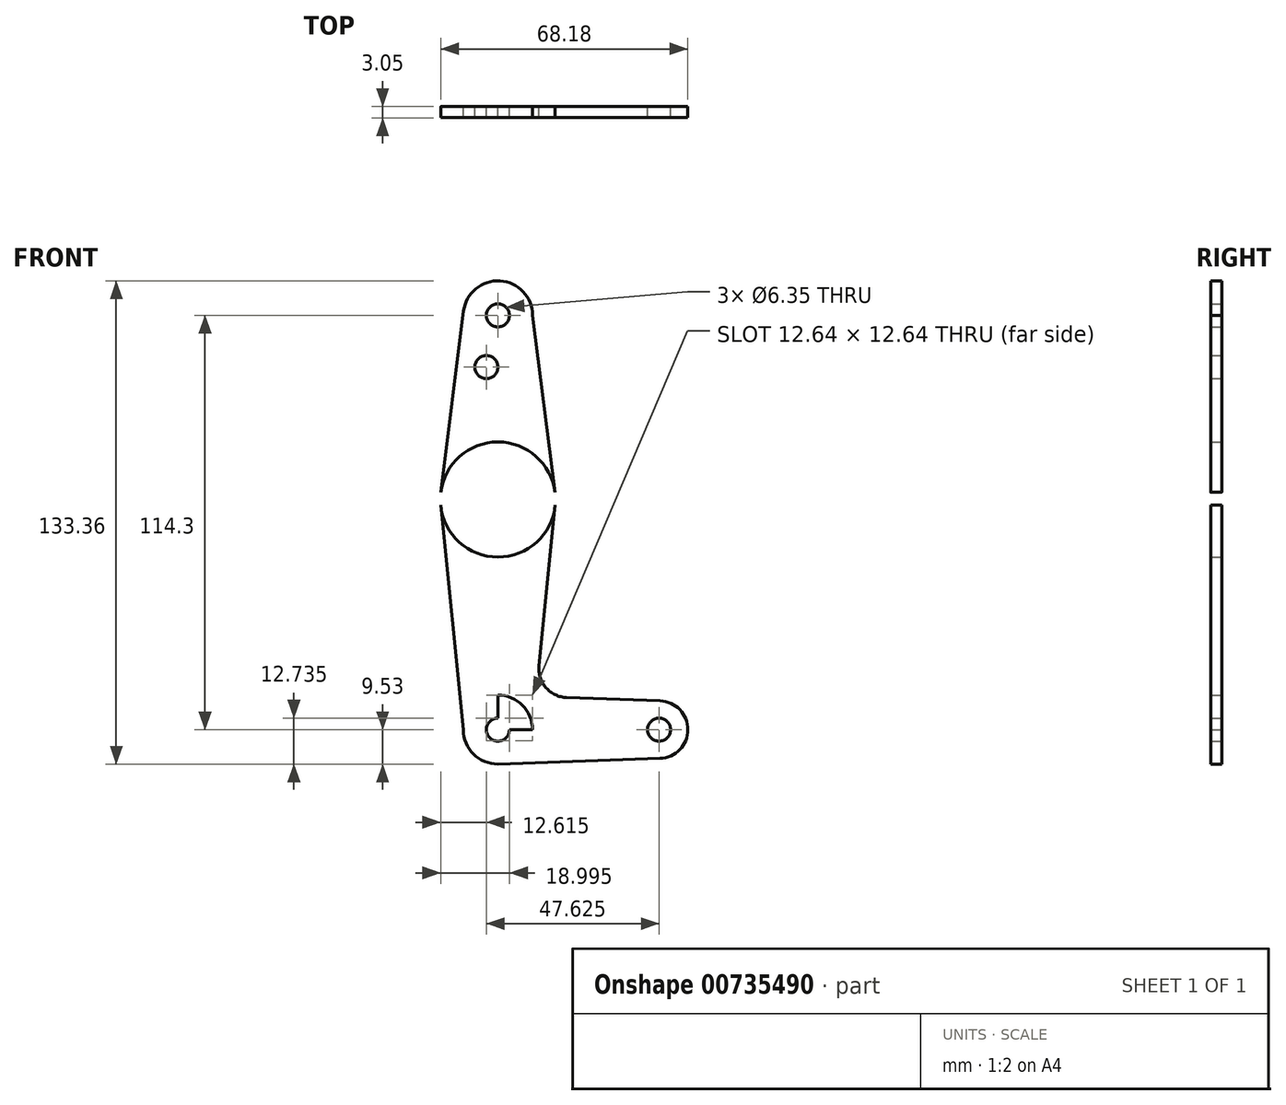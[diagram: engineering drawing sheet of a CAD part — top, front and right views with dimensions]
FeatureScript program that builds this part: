
annotation { "Feature Type Name" : "Feature", "Feature Type Description" : "" }
export const myFeature = defineFeature(function(context is Context, id is Id, definition is map)
    precondition{}
    {
        {
            var Q0;
            Q0=qCreatedBy(makeId("Front.planeOp"),FACE);
            var sketch = newSketch(context, id + "F0", { "sketchPlane" : qUnion([Q0])});
            skLineSegment(sketch, "E0", {"start": v(0, 0) * mm, "end": v(0, 114.3) * mm});
            skLineSegment(sketch, "E1", {"start": v(0, 114.3) * mm, "end": v(0, 0) * mm});
            skLineSegment(sketch, "E2", {"start": v(0, 0) * mm, "end": v(44.45, 0) * mm});
            skCircle(sketch, "E3", {"center": v(0, 0) * mm, "radius": 9.53 * mm});
            skCircle(sketch, "E4", {"center": v(0, 63.5) * mm, "radius": 15.88 * mm});
            skCircle(sketch, "E5", {"center": v(0, 114.3) * mm, "radius": 9.53 * mm});
            skCircle(sketch, "E6", {"center": v(44.45, 0) * mm, "radius": 7.94 * mm});
            skLineSegment(sketch, "E7", {"start": v(9.52, 114.3) * mm, "end": v(15.75, 65.5) * mm});
            skLineSegment(sketch, "E8", {"start": v(15.8, 61.9) * mm, "end": v(11.34, 17.59) * mm});
            skPoint(sketch, "E9", {"position": v(0, 9.53) * mm});
            skLineSegment(sketch, "E10", {"start": v(18.97, 8.85) * mm, "end": v(44.73, 7.93) * mm});
            skLineSegment(sketch, "E11", {"start": v(0, -9.53) * mm, "end": v(44.73, -7.93) * mm});
            skLineSegment(sketch, "E12", {"start": v(-9.45, 115.5) * mm, "end": v(-15.75, 65.48) * mm});
            skLineSegment(sketch, "E13", {"start": v(-9.52, 0) * mm, "end": v(-15.8, 61.9) * mm});
            skCircle(sketch, "E14", {"center": v(0, 114.3) * mm, "radius": 3.18 * mm});
            skCircle(sketch, "E15", {"center": v(0, 63.5) * mm, "radius": 3.18 * mm});
            skCircle(sketch, "E16", {"center": v(0, 0) * mm, "radius": 3.18 * mm});
            skCircle(sketch, "E17", {"center": v(44.45, 0) * mm, "radius": 3.18 * mm});
            skCircle(sketch, "E18", {"center": v(-3.18, 100.03) * mm, "radius": 3.18 * mm});
            skArc(sketch, "E19.filletArc", {"start": v(11.34, 17.59) * mm, "mid": v(13.26, 11.57) * mm, "end": v(18.97, 8.85) * mm});
            skSolve(sketch);
        }
        {
            var Q0;
            {var subQ0=sQuery(id+"F0.wireOp",EDGE,"E4");var subQ2=sQuery(id+"F0.wireOp",EDGE,"E1");var subQ5=makeQuery(id+"F0.imprint","INTERSECT",VERTEX,{"disambiguationData":[OD(0.0)],"derivedFrom":[subQ2,subQ0]});Q0=makeQuery(id+"F0.imprint","IMPRINT",FACE,{"disambiguationData":[TD([[makeQuery(id+"F0.imprint","IMPRINT",EDGE,{"disambiguationData":[TD([[subQ5,-1.0]])],"derivedFrom":subQ2}),1.0]])]});}
            var Q1;
            {var subQ0=sQuery(id+"F0.wireOp",EDGE,"E12");Q1=makeQuery(id+"F0.imprint","IMPRINT",FACE,{"disambiguationData":[TD([[makeQuery(id+"F0.imprint","IMPRINT",EDGE,{"derivedFrom":subQ0}),1.0]])]});}
            var Q2;
            {var subQ0=sQuery(id+"F0.wireOp",EDGE,"E6");var subQ1=sQuery(id+"F0.wireOp",EDGE,"E2");var subQ2=makeQuery(id+"F0.imprint","INTERSECT",VERTEX,{"derivedFrom":[subQ1,subQ0]});Q2=makeQuery(id+"F0.imprint","IMPRINT",FACE,{"disambiguationData":[TD([[makeQuery(id+"F0.imprint","IMPRINT",EDGE,{"disambiguationData":[TD([[subQ2,1.0]])],"derivedFrom":subQ1}),-1.0]])]});}
            var Q3;
            Q3=makeQuery(id+"F0.imprint","IMPRINT",FACE,{"disambiguationData":[TD([[makeQuery(id+"F0.imprint","IMPRINT",EDGE,{"derivedFrom":sQuery(id+"F0.wireOp",EDGE,"E17")}),-1.0]])]});
            var Q4;
            {var subQ5=sQuery(id+"F0.wireOp",EDGE,"E8");Q4=makeQuery(id+"F0.imprint","IMPRINT",FACE,{"disambiguationData":[TD([[makeQuery(id+"F0.imprint","IMPRINT",EDGE,{"derivedFrom":subQ5}),-1.0]])]});}
            var Q5;
            {var subQ0=sQuery(id+"F0.wireOp",EDGE,"E7");Q5=makeQuery(id+"F0.imprint","IMPRINT",FACE,{"disambiguationData":[TD([[makeQuery(id+"F0.imprint","IMPRINT",EDGE,{"derivedFrom":subQ0}),-1.0]])]});}
            var Q6;
            Q6=makeQuery(id+"F0.imprint","IMPRINT",FACE,{"disambiguationData":[TD([[makeQuery(id+"F0.imprint","IMPRINT",EDGE,{"derivedFrom":sQuery(id+"F0.wireOp",EDGE,"E14")}),-1.0]])]});
            var Q7;
            {var subQ5=sQuery(id+"F0.wireOp",EDGE,"E13");Q7=makeQuery(id+"F0.imprint","IMPRINT",FACE,{"disambiguationData":[TD([[makeQuery(id+"F0.imprint","IMPRINT",EDGE,{"derivedFrom":subQ5}),-1.0]])]});}
            var Q8;
            {var subQ1=sQuery(id+"F0.wireOp",EDGE,"E3");var subQ4=sQuery(id+"F0.wireOp",EDGE,"E1");var subQ5=makeQuery(id+"F0.imprint","INTERSECT",VERTEX,{"derivedFrom":[subQ4,subQ1]});Q8=makeQuery(id+"F0.imprint","IMPRINT",FACE,{"disambiguationData":[TD([[makeQuery(id+"F0.imprint","IMPRINT",EDGE,{"disambiguationData":[TD([[subQ5,-1.0]])],"derivedFrom":subQ4}),-1.0]])]});}
            var Q9;
            {var subQ0=sQuery(id+"F0.wireOp",EDGE,"E4");var subQ4=sQuery(id+"F0.wireOp",EDGE,"E1");var subQ7=makeQuery(id+"F0.imprint","INTERSECT",VERTEX,{"disambiguationData":[OD(0.0)],"derivedFrom":[subQ4,subQ0]});Q9=makeQuery(id+"F0.imprint","IMPRINT",FACE,{"disambiguationData":[TD([[makeQuery(id+"F0.imprint","IMPRINT",EDGE,{"disambiguationData":[TD([[subQ7,-1.0]])],"derivedFrom":subQ4}),-1.0]])]});}
            var Q10;
            {var subQ0=sQuery(id+"F0.wireOp",EDGE,"E11");var subQ1=sQuery(id+"F0.wireOp",EDGE,"E3");var subQ2=makeQuery(id+"F0.imprint","INTERSECT",VERTEX,{"disambiguationData":[OD(0.0)],"derivedFrom":[subQ1,subQ0]});Q10=makeQuery(id+"F0.imprint","IMPRINT",FACE,{"disambiguationData":[TD([[makeQuery(id+"F0.imprint","IMPRINT",EDGE,{"disambiguationData":[TD([[subQ2,-1.0]])],"derivedFrom":subQ1}),1.0]])]});}
            var Q11;
            {var subQ0=sQuery(id+"F0.wireOp",EDGE,"E3");var subQ1=sQuery(id+"F0.wireOp",EDGE,"E1");var subQ2=makeQuery(id+"F0.imprint","INTERSECT",VERTEX,{"derivedFrom":[subQ1,subQ0]});Q11=makeQuery(id+"F0.imprint","IMPRINT",FACE,{"disambiguationData":[TD([[makeQuery(id+"F0.imprint","IMPRINT",EDGE,{"disambiguationData":[TD([[subQ2,-1.0]])],"derivedFrom":subQ1}),1.0]])]});}
            extrude(context, id + "F1", {"entities" : qUnion([Q0, Q1, Q2, Q3, Q4, Q5, Q6, Q7, Q8, Q9, Q10, Q11]), "depth" : 3.05 * mm, "offsetDistance" : 25.4 * mm});
        }
    });
